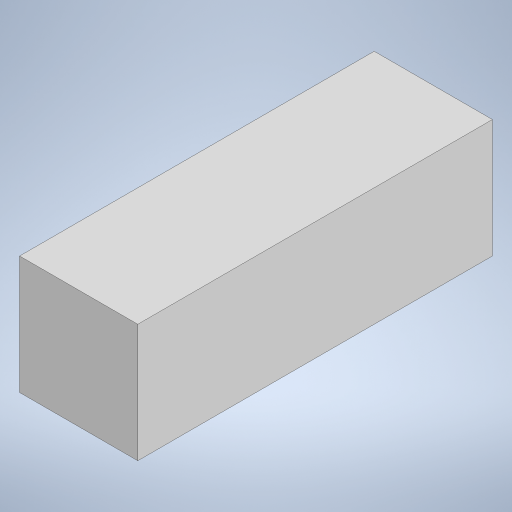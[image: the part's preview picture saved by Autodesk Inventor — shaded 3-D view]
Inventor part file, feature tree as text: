
AUTODESK INVENTOR PART (.ipt)
format: ipt  version: 2023 (Build 270158000, 158)  size: 172,544 bytes
history: native  units: in
note: dims shown in document units (in); Inventor stores cm internally (conversion verified against a paired STEP export)
features: extrude x1, sketch x1
ambient origin geometry x8: Origin, YZ Plane, XZ Plane, XY Plane, X Axis, Y Axis, Z Axis, Center Point
bodies: Solid1 (feature_tree)
feature tree (2):
  extrude  "Extrusion1"  Depth=3.0in
  sketch  "Sketch1"  dims[d0=1.0in d1=3.0in d2=1.0in d3=0.0in]
